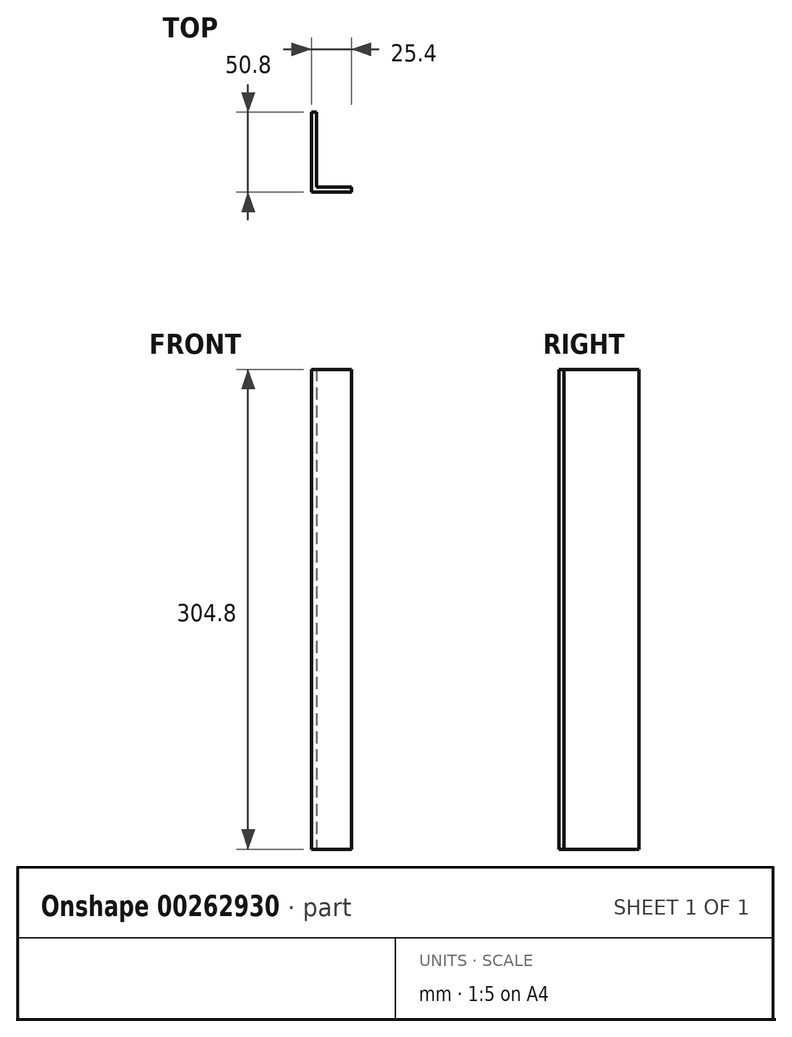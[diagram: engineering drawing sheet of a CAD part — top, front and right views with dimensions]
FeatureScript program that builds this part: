
annotation { "Feature Type Name" : "Feature", "Feature Type Description" : "" }
export const myFeature = defineFeature(function(context is Context, id is Id, definition is map)
    precondition{}
    {
        {
            var Q0;
            Q0=qCreatedBy(makeId("Top.planeOp"),FACE);
            var sketch = newSketch(context, id + "F0", { "sketchPlane" : qUnion([Q0])});
            skLineSegment(sketch, "E0", {"start": v(0, 50.8) * mm, "end": v(0, 0) * mm});
            skLineSegment(sketch, "E1", {"start": v(0, 0) * mm, "end": v(25.4, 0) * mm});
            skLineSegment(sketch, "E2", {"start": v(25.4, 0) * mm, "end": v(25.4, 3.18) * mm});
            skLineSegment(sketch, "E3", {"start": v(25.4, 3.18) * mm, "end": v(3.18, 3.17) * mm});
            skLineSegment(sketch, "E4", {"start": v(3.18, 3.17) * mm, "end": v(3.18, 50.8) * mm});
            skLineSegment(sketch, "E5", {"start": v(3.18, 50.8) * mm, "end": v(0, 50.8) * mm});
            skSolve(sketch);
        }
        {
            var Q0;
            Q0=makeQuery(id+"F0.imprint","IMPRINT",FACE,{"disambiguationData":[TD([[makeQuery(id+"F0.imprint","IMPRINT",EDGE,{"derivedFrom":sQuery(id+"F0.wireOp",EDGE,"E0")}),1.0]])]});
            extrude(context, id + "F1", {"entities" : qUnion([Q0]), "depth" : 304.8 * mm});
        }
    });
